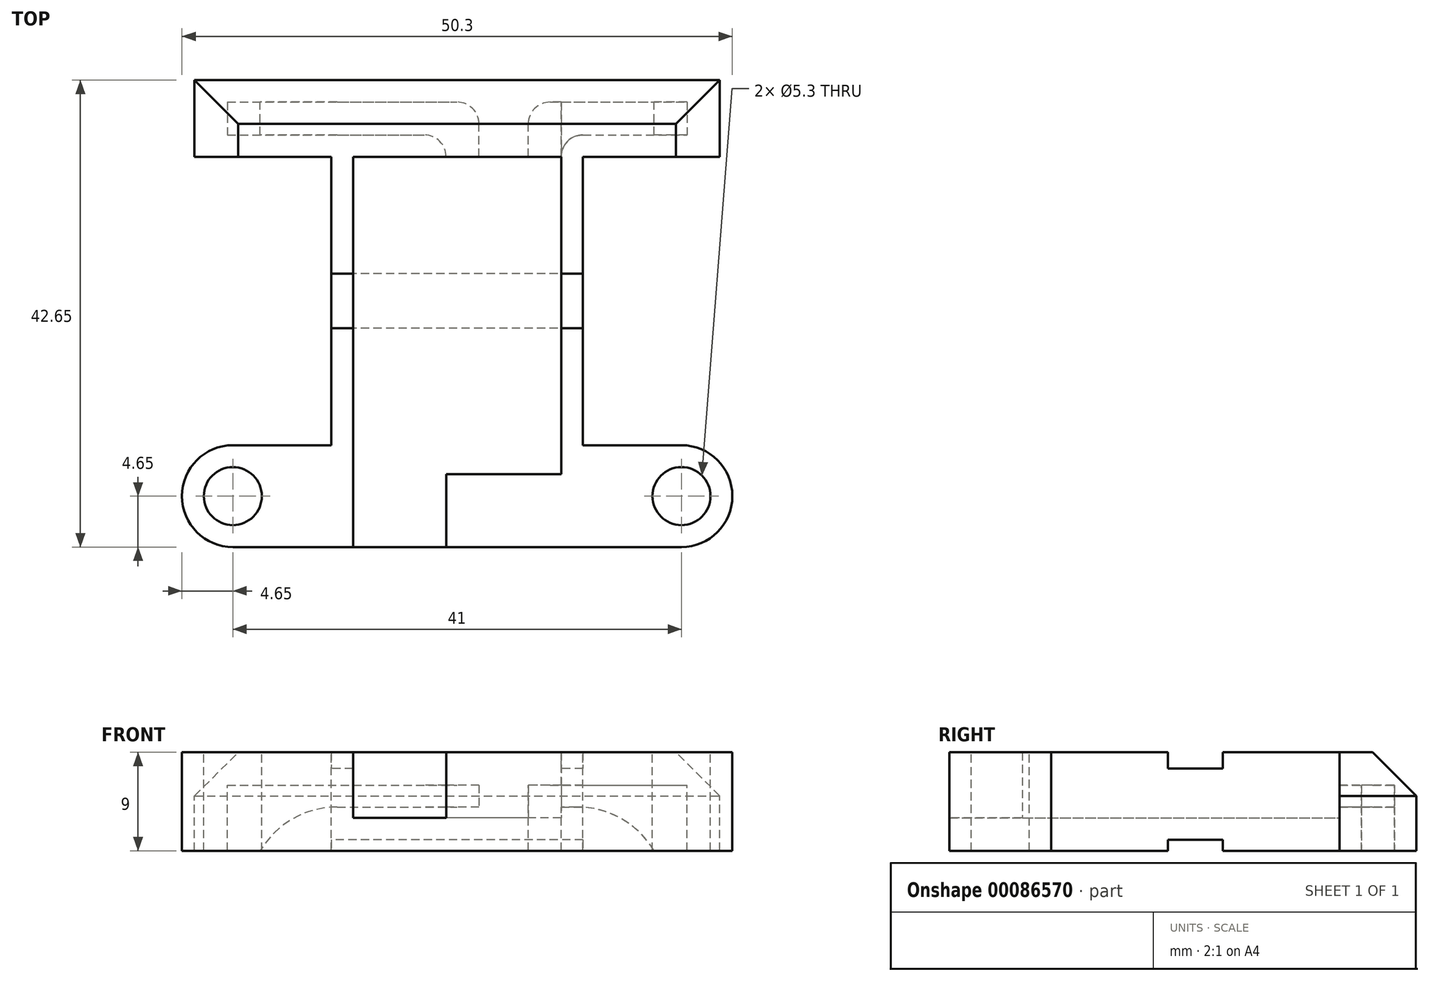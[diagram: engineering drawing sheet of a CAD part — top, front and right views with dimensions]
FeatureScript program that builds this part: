
annotation { "Feature Type Name" : "Feature", "Feature Type Description" : "" }
export const myFeature = defineFeature(function(context is Context, id is Id, definition is map)
    precondition{}
    {
        {
            var Q0;
            Q0=qCreatedBy(makeId("Top.planeOp"),FACE);
            var sketch = newSketch(context, id + "F0", { "sketchPlane" : qUnion([Q0])});
            skLineSegment(sketch, "E0.bottom", {"start": v(9.5, -14.5) * mm, "end": v(-1, -14.5) * mm});
            skLineSegment(sketch, "E0.top", {"start": v(9.5, 14.5) * mm, "end": v(-9.5, 14.5) * mm});
            skLineSegment(sketch, "E0.left", {"start": v(9.5, -14.5) * mm, "end": v(9.5, 14.5) * mm});
            skLineSegment(sketch, "E0.right", {"start": v(-9.5, -21.15) * mm, "end": v(-9.5, 14.5) * mm});
            skPoint(sketch, "E0.middle", {"position": v(0, 0) * mm});
            skLineSegment(sketch, "E1.right", {"start": v(-1, -14.5) * mm, "end": v(-1, -21.15) * mm});
            skLineSegment(sketch, "E2.bottom", {"start": v(-1, 19.5) * mm, "end": v(2, 19.5) * mm});
            skLineSegment(sketch, "E2.top", {"start": v(-1, 14.5) * mm, "end": v(2, 14.5) * mm});
            skLineSegment(sketch, "E2.left", {"start": v(-1, 19.5) * mm, "end": v(-1, 14.5) * mm});
            skLineSegment(sketch, "E2.right", {"start": v(2, 19.5) * mm, "end": v(2, 14.5) * mm});
            skLineSegment(sketch, "E3.bottom", {"start": v(9.5, 14.5) * mm, "end": v(6.5, 14.5) * mm});
            skLineSegment(sketch, "E3.top", {"start": v(9.5, 19.5) * mm, "end": v(6.5, 19.5) * mm});
            skLineSegment(sketch, "E3.left", {"start": v(9.5, 14.5) * mm, "end": v(9.5, 19.5) * mm});
            skLineSegment(sketch, "E3.right", {"start": v(6.5, 14.5) * mm, "end": v(6.5, 19.5) * mm});
            skLineSegment(sketch, "E4.1", {"start": v(20.5, -21.15) * mm, "end": v(-20.5, -21.15) * mm});
            skLineSegment(sketch, "E4.2", {"start": v(11.5, -11.85) * mm, "end": v(11.5, 14.5) * mm});
            skLineSegment(sketch, "E4.4", {"start": v(-11.5, -11.85) * mm, "end": v(-11.5, 14.5) * mm});
            skCircle(sketch, "E5", {"center": v(20.5, -16.5) * mm, "radius": 2.65 * mm});
            skArc(sketch, "E6.0", {"start": v(20.5, -21.15) * mm, "mid": v(25.15, -16.5) * mm, "end": v(20.5, -11.85) * mm});
            skLineSegment(sketch, "E7", {"start": v(11.5, -11.85) * mm, "end": v(20.5, -11.85) * mm});
            skArc(sketch, "E8.MirrorCS", {"start": v(-20.5, -21.15) * mm, "mid": v(-25.15, -16.5) * mm, "end": v(-20.5, -11.85) * mm});
            skCircle(sketch, "E9.MirrorC", {"center": v(-20.5, -16.5) * mm, "radius": 2.65 * mm});
            skLineSegment(sketch, "E10.MirrorCS", {"start": v(-11.5, -11.85) * mm, "end": v(-20.5, -11.85) * mm});
            skLineSegment(sketch, "E11.top", {"start": v(11.5, 14.5) * mm, "end": v(24, 14.5) * mm});
            skLineSegment(sketch, "E11.right", {"start": v(24, 21.5) * mm, "end": v(24, 14.5) * mm});
            skLineSegment(sketch, "E12.MirrorCS", {"start": v(-11.5, 14.5) * mm, "end": v(-24, 14.5) * mm});
            skLineSegment(sketch, "E13.MirrorCS", {"start": v(-24, 21.5) * mm, "end": v(-24, 14.5) * mm});
            skLineSegment(sketch, "E14.MirrorCS", {"start": v(24, 21.5) * mm, "end": v(-24, 21.5) * mm});
            skLineSegment(sketch, "E15.bottom", {"start": v(21, 16.5) * mm, "end": v(18, 16.5) * mm});
            skLineSegment(sketch, "E15.top", {"start": v(21, 19.5) * mm, "end": v(18, 19.5) * mm});
            skLineSegment(sketch, "E15.left", {"start": v(21, 16.5) * mm, "end": v(21, 19.5) * mm});
            skLineSegment(sketch, "E15.right", {"start": v(18, 16.5) * mm, "end": v(18, 19.5) * mm});
            skPoint(sketch, "E15.middle", {"position": v(19.5, 18) * mm});
            skLineSegment(sketch, "E16.MirrorCS", {"start": v(-21, 19.5) * mm, "end": v(-18, 19.5) * mm});
            skLineSegment(sketch, "E17.MirrorCS", {"start": v(-21, 16.5) * mm, "end": v(-21, 19.5) * mm});
            skLineSegment(sketch, "E18.MirrorCS", {"start": v(-21, 16.5) * mm, "end": v(-18, 16.5) * mm});
            skLineSegment(sketch, "E19.MirrorCS", {"start": v(-18, 16.5) * mm, "end": v(-18, 19.5) * mm});
            skPoint(sketch, "E20.MirrorP", {"position": v(-19.5, 18) * mm});
            skPoint(sketch, "E21", {"position": v(24, 18) * mm});
            skSolve(sketch);
        }
        {
            var Q0;
            {var subQ2=sQuery(id+"F0.wireOp",EDGE,"E12.MirrorCS");Q0=makeQuery(id+"F0.imprint","IMPRINT",FACE,{"disambiguationData":[TD([[makeQuery(id+"F0.imprint","IMPRINT",EDGE,{"derivedFrom":subQ2}),-1.0]])]});}
            var Q1;
            Q1=makeQuery(id+"F0.imprint","IMPRINT",FACE,{"disambiguationData":[TD([[makeQuery(id+"F0.imprint","IMPRINT",EDGE,{"derivedFrom":sQuery(id+"F0.wireOp",EDGE,"E0.bottom")}),1.0]])]});
            var Q2;
            Q2=makeQuery(id+"F0.imprint","IMPRINT",FACE,{"disambiguationData":[TD([[makeQuery(id+"F0.imprint","IMPRINT",EDGE,{"derivedFrom":sQuery(id+"F0.wireOp",EDGE,"E0.bottom")}),-1.0]])]});
            var Q3;
            Q3=makeQuery(id+"F0.imprint","IMPRINT",FACE,{"disambiguationData":[TD([[makeQuery(id+"F0.imprint","IMPRINT",EDGE,{"derivedFrom":sQuery(id+"F0.wireOp",EDGE,"E11.bottom")}),-1.0]])]});
            var Q4;
            Q4=makeQuery(id+"F0.imprint","IMPRINT",FACE,{"disambiguationData":[TD([[makeQuery(id+"F0.imprint","IMPRINT",EDGE,{"derivedFrom":sQuery(id+"F0.wireOp",EDGE,"E5")}),-1.0]])]});
            var Q5;
            {var subQ2=sQuery(id+"F0.wireOp",EDGE,"E4.0");Q5=makeQuery(id+"F0.imprint","IMPRINT",FACE,{"disambiguationData":[TD([[makeQuery(id+"F0.imprint","IMPRINT",EDGE,{"derivedFrom":subQ2}),-1.0]])]});}
            var Q6;
            Q6=makeQuery(id+"F0.imprint","IMPRINT",FACE,{"disambiguationData":[TD([[makeQuery(id+"F0.imprint","IMPRINT",EDGE,{"derivedFrom":sQuery(id+"F0.wireOp",EDGE,"E2.bottom")}),-1.0]])]});
            var Q7;
            Q7=makeQuery(id+"F0.imprint","IMPRINT",FACE,{"disambiguationData":[TD([[makeQuery(id+"F0.imprint","IMPRINT",EDGE,{"derivedFrom":sQuery(id+"F0.wireOp",EDGE,"E3.bottom")}),-1.0]])]});
            var Q8;
            {var subQ0=sQuery(id+"F0.wireOp",EDGE,"E8.MirrorCS");Q8=makeQuery(id+"F0.imprint","IMPRINT",FACE,{"disambiguationData":[TD([[makeQuery(id+"F0.imprint","IMPRINT",EDGE,{"derivedFrom":subQ0}),-1.0]])]});}
            extrude(context, id + "F1", {"entities" : qUnion([Q0, Q1, Q2, Q3, Q4, Q5, Q6, Q7, Q8]), "oppositeDirection" : true, "depth" : 3 * mm});
        }
        {
            var Q0;
            Q0=makeQuery(id+"F0.imprint","IMPRINT",FACE,{"disambiguationData":[TD([[makeQuery(id+"F0.imprint","IMPRINT",EDGE,{"derivedFrom":sQuery(id+"F0.wireOp",EDGE,"E0.bottom")}),1.0]])]});
            var Q1;
            {var subQ2=sQuery(id+"F0.wireOp",EDGE,"E12.MirrorCS");Q1=makeQuery(id+"F0.imprint","IMPRINT",FACE,{"disambiguationData":[TD([[makeQuery(id+"F0.imprint","IMPRINT",EDGE,{"derivedFrom":subQ2}),-1.0]])]});}
            var Q2;
            Q2=makeQuery(id+"F0.imprint","IMPRINT",FACE,{"disambiguationData":[TD([[makeQuery(id+"F0.imprint","IMPRINT",EDGE,{"derivedFrom":sQuery(id+"F0.wireOp",EDGE,"E11.bottom")}),-1.0]])]});
            var Q3;
            {var subQ2=sQuery(id+"F0.wireOp",EDGE,"E4.0");Q3=makeQuery(id+"F0.imprint","IMPRINT",FACE,{"disambiguationData":[TD([[makeQuery(id+"F0.imprint","IMPRINT",EDGE,{"derivedFrom":subQ2}),-1.0]])]});}
            var Q4;
            Q4=makeQuery(id+"F0.imprint","IMPRINT",FACE,{"disambiguationData":[TD([[makeQuery(id+"F0.imprint","IMPRINT",EDGE,{"derivedFrom":sQuery(id+"F0.wireOp",EDGE,"E5")}),-1.0]])]});
            var Q5;
            {var subQ0=sQuery(id+"F0.wireOp",EDGE,"E8.MirrorCS");Q5=makeQuery(id+"F0.imprint","IMPRINT",FACE,{"disambiguationData":[TD([[makeQuery(id+"F0.imprint","IMPRINT",EDGE,{"derivedFrom":subQ0}),-1.0]])]});}
            extrude(context, id + "F2", {"entities" : qUnion([Q0, Q1, Q2, Q3, Q4, Q5]), "operationType" : NewBodyOperationType.ADD, "depth" : 6 * mm});
        }
        {
            var Q0;
            Q0=makeQuery(id+"F2.opExtrude","CAP_FACE",FACE,{"disambiguationData":[OSD([sQuery(id+"F0.wireOp",EDGE,"E0.bottom"),sQuery(id+"F0.wireOp",EDGE,"E0.top"),sQuery(id+"F0.wireOp",EDGE,"E0.left"),sQuery(id+"F0.wireOp",EDGE,"E0.right"),sQuery(id+"F0.wireOp",EDGE,"E1.left"),sQuery(id+"F0.wireOp",EDGE,"E1.right"),sQuery(id+"F0.wireOp",EDGE,"E2.bottom"),sQuery(id+"F0.wireOp",EDGE,"E2.left"),sQuery(id+"F0.wireOp",EDGE,"E2.right"),sQuery(id+"F0.wireOp",EDGE,"E3.top"),sQuery(id+"F0.wireOp",EDGE,"E3.left"),sQuery(id+"F0.wireOp",EDGE,"E3.right"),sQuery(id+"F0.wireOp",EDGE,"E4.1"),sQuery(id+"F0.wireOp",EDGE,"E4.2"),sQuery(id+"F0.wireOp",EDGE,"E4.4"),sQuery(id+"F0.wireOp",EDGE,"QdOgvTVK-R7uH-Gxik-RYz1-CrQYq477OOmn"),sQuery(id+"F0.wireOp",EDGE,"E5"),sQuery(id+"F0.wireOp",EDGE,"E6.0"),sQuery(id+"F0.wireOp",EDGE,"E7"),sQuery(id+"F0.wireOp",EDGE,"16d9e2e4-1f67-46e0-b017-a798e0a491060.MirrorCS"),sQuery(id+"F0.wireOp",EDGE,"E8.MirrorCS"),sQuery(id+"F0.wireOp",EDGE,"E9.MirrorC"),sQuery(id+"F0.wireOp",EDGE,"E10.MirrorCS"),sQuery(id+"F0.wireOp",EDGE,"E11.bottom"),sQuery(id+"F0.wireOp",EDGE,"E11.top"),sQuery(id+"F0.wireOp",EDGE,"E11.right"),sQuery(id+"F0.wireOp",EDGE,"mg0W0evk-kMHr-gRv2-KS9r-GgxPjsrzOnwv.bottom"),sQuery(id+"F0.wireOp",EDGE,"mg0W0evk-kMHr-gRv2-KS9r-GgxPjsrzOnwv.top"),sQuery(id+"F0.wireOp",EDGE,"mg0W0evk-kMHr-gRv2-KS9r-GgxPjsrzOnwv.left"),sQuery(id+"F0.wireOp",EDGE,"mg0W0evk-kMHr-gRv2-KS9r-GgxPjsrzOnwv.right"),sQuery(id+"F0.wireOp",EDGE,"E12.MirrorCS"),sQuery(id+"F0.wireOp",EDGE,"E13.MirrorCS"),sQuery(id+"F0.wireOp",EDGE,"E14.MirrorCS"),sQuery(id+"F0.wireOp",EDGE,"11edd65b-5519-47c1-b7c5-a84d8e4c1fdb0.MirrorCS"),sQuery(id+"F0.wireOp",EDGE,"769f5433-8976-4236-af09-d3d3242829100.MirrorCS"),sQuery(id+"F0.wireOp",EDGE,"1cde3c8c-1ea3-4720-a5be-defc2df602b40.MirrorCS"),sQuery(id+"F0.wireOp",EDGE,"8eaebaa9-42e2-4e42-8a77-1a7deb14469b0.MirrorCS")])],"isStart":false});
            cPlane(context, id + "F3", {"entities" : qUnion([Q0]), "cplaneType" : CPlaneType.OFFSET, "offset" : 4 * mm, "oppositeDirection" : true, "width" : 150 * mm, "height" : 150 * mm});
        }
        {
            var Q0;
            Q0=qCreatedBy(id+"F3.planeOp",FACE);
            var sketch = newSketch(context, id + "F4", { "sketchPlane" : qUnion([Q0])});
            skLineSegment(sketch, "E22.bottom", {"start": v(-21, 19.5) * mm, "end": v(2, 19.5) * mm});
            skLineSegment(sketch, "E22.top", {"start": v(-21, 16.5) * mm, "end": v(2, 16.5) * mm});
            skLineSegment(sketch, "E22.left", {"start": v(-21, 19.5) * mm, "end": v(-21, 16.5) * mm});
            skLineSegment(sketch, "E22.right", {"start": v(2, 19.5) * mm, "end": v(2, 16.5) * mm});
            skLineSegment(sketch, "E23.bottom", {"start": v(6.5, 19.5) * mm, "end": v(21, 19.5) * mm});
            skLineSegment(sketch, "E23.top", {"start": v(6.5, 16.5) * mm, "end": v(21, 16.5) * mm});
            skLineSegment(sketch, "E23.left", {"start": v(6.5, 19.5) * mm, "end": v(6.5, 16.5) * mm});
            skLineSegment(sketch, "E23.right", {"start": v(21, 19.5) * mm, "end": v(21, 16.5) * mm});
            skSolve(sketch);
        }
        {
            var Q0;
            Q0=makeQuery(id+"F4.imprint","IMPRINT",FACE,{"disambiguationData":[TD([[makeQuery(id+"F4.imprint","IMPRINT",EDGE,{"derivedFrom":sQuery(id+"F4.wireOp",EDGE,"E22.bottom")}),-1.0]])]});
            var Q1;
            Q1=makeQuery(id+"F4.imprint","IMPRINT",FACE,{"disambiguationData":[TD([[makeQuery(id+"F4.imprint","IMPRINT",EDGE,{"derivedFrom":sQuery(id+"F4.wireOp",EDGE,"E23.bottom")}),-1.0]])]});
            extrude(context, id + "F5", {"entities" : qUnion([Q0, Q1]), "operationType" : NewBodyOperationType.REMOVE, "endBound" : BoundingType.SYMMETRIC, "oppositeDirection" : true, "depth" : 2 * mm});
        }
        {
            var Q0;
            Q0=makeQuery(id+"F2.opExtrude","CAP_FACE",FACE,{"disambiguationData":[OSD([sQuery(id+"F0.wireOp",EDGE,"E0.bottom"),sQuery(id+"F0.wireOp",EDGE,"E0.top"),sQuery(id+"F0.wireOp",EDGE,"E0.left"),sQuery(id+"F0.wireOp",EDGE,"E0.right"),sQuery(id+"F0.wireOp",EDGE,"E1.left"),sQuery(id+"F0.wireOp",EDGE,"E1.right"),sQuery(id+"F0.wireOp",EDGE,"E2.bottom"),sQuery(id+"F0.wireOp",EDGE,"E2.left"),sQuery(id+"F0.wireOp",EDGE,"E2.right"),sQuery(id+"F0.wireOp",EDGE,"E3.top"),sQuery(id+"F0.wireOp",EDGE,"E3.left"),sQuery(id+"F0.wireOp",EDGE,"E3.right"),sQuery(id+"F0.wireOp",EDGE,"E4.1"),sQuery(id+"F0.wireOp",EDGE,"E4.2"),sQuery(id+"F0.wireOp",EDGE,"E4.4"),sQuery(id+"F0.wireOp",EDGE,"QdOgvTVK-R7uH-Gxik-RYz1-CrQYq477OOmn"),sQuery(id+"F0.wireOp",EDGE,"E5"),sQuery(id+"F0.wireOp",EDGE,"E6.0"),sQuery(id+"F0.wireOp",EDGE,"E7"),sQuery(id+"F0.wireOp",EDGE,"16d9e2e4-1f67-46e0-b017-a798e0a491060.MirrorCS"),sQuery(id+"F0.wireOp",EDGE,"E8.MirrorCS"),sQuery(id+"F0.wireOp",EDGE,"E9.MirrorC"),sQuery(id+"F0.wireOp",EDGE,"E10.MirrorCS"),sQuery(id+"F0.wireOp",EDGE,"E11.bottom"),sQuery(id+"F0.wireOp",EDGE,"E11.top"),sQuery(id+"F0.wireOp",EDGE,"E11.right"),sQuery(id+"F0.wireOp",EDGE,"mg0W0evk-kMHr-gRv2-KS9r-GgxPjsrzOnwv.bottom"),sQuery(id+"F0.wireOp",EDGE,"mg0W0evk-kMHr-gRv2-KS9r-GgxPjsrzOnwv.top"),sQuery(id+"F0.wireOp",EDGE,"mg0W0evk-kMHr-gRv2-KS9r-GgxPjsrzOnwv.left"),sQuery(id+"F0.wireOp",EDGE,"mg0W0evk-kMHr-gRv2-KS9r-GgxPjsrzOnwv.right"),sQuery(id+"F0.wireOp",EDGE,"E12.MirrorCS"),sQuery(id+"F0.wireOp",EDGE,"E13.MirrorCS"),sQuery(id+"F0.wireOp",EDGE,"E14.MirrorCS"),sQuery(id+"F0.wireOp",EDGE,"11edd65b-5519-47c1-b7c5-a84d8e4c1fdb0.MirrorCS"),sQuery(id+"F0.wireOp",EDGE,"769f5433-8976-4236-af09-d3d3242829100.MirrorCS"),sQuery(id+"F0.wireOp",EDGE,"1cde3c8c-1ea3-4720-a5be-defc2df602b40.MirrorCS"),sQuery(id+"F0.wireOp",EDGE,"8eaebaa9-42e2-4e42-8a77-1a7deb14469b0.MirrorCS")])],"isStart":false});
            var sketch = newSketch(context, id + "F6", { "sketchPlane" : qUnion([Q0])});
            skLineSegment(sketch, "E24.bottom", {"start": v(18, 19.5) * mm, "end": v(21, 19.5) * mm});
            skLineSegment(sketch, "E24.top", {"start": v(18, 16.5) * mm, "end": v(21, 16.5) * mm});
            skLineSegment(sketch, "E24.left", {"start": v(18, 19.5) * mm, "end": v(18, 16.5) * mm});
            skLineSegment(sketch, "E24.right", {"start": v(21, 19.5) * mm, "end": v(21, 16.5) * mm});
            skLineSegment(sketch, "E25.MirrorCS", {"start": v(-18, 19.5) * mm, "end": v(-18, 16.5) * mm});
            skLineSegment(sketch, "E26.MirrorCS", {"start": v(-18, 19.5) * mm, "end": v(-21, 19.5) * mm});
            skLineSegment(sketch, "E27.MirrorCS", {"start": v(-21, 19.5) * mm, "end": v(-21, 16.5) * mm});
            skLineSegment(sketch, "E28.MirrorCS", {"start": v(-18, 16.5) * mm, "end": v(-21, 16.5) * mm});
            skLineSegment(sketch, "E29.bottom", {"start": v(-1, 19.5) * mm, "end": v(2, 19.5) * mm});
            skLineSegment(sketch, "E29.top", {"start": v(-1, 14.5) * mm, "end": v(2, 14.5) * mm});
            skLineSegment(sketch, "E29.left", {"start": v(-1, 19.5) * mm, "end": v(-1, 14.5) * mm});
            skLineSegment(sketch, "E29.right", {"start": v(2, 19.5) * mm, "end": v(2, 14.5) * mm});
            skLineSegment(sketch, "E30.bottom", {"start": v(6.5, 19.5) * mm, "end": v(9.5, 19.5) * mm});
            skLineSegment(sketch, "E30.top", {"start": v(6.5, 14.5) * mm, "end": v(9.5, 14.5) * mm});
            skLineSegment(sketch, "E30.left", {"start": v(6.5, 19.5) * mm, "end": v(6.5, 14.5) * mm});
            skLineSegment(sketch, "E30.right", {"start": v(9.5, 19.5) * mm, "end": v(9.5, 14.5) * mm});
            skSolve(sketch);
        }
        {
            var Q0;
            Q0=makeQuery(id+"F0.imprint","IMPRINT",FACE,{"disambiguationData":[TD([[makeQuery(id+"F0.imprint","IMPRINT",EDGE,{"derivedFrom":sQuery(id+"F0.wireOp",EDGE,"E2.bottom")}),-1.0]])]});
            var Q1;
            Q1=makeQuery(id+"F0.imprint","IMPRINT",FACE,{"disambiguationData":[TD([[makeQuery(id+"F0.imprint","IMPRINT",EDGE,{"derivedFrom":sQuery(id+"F0.wireOp",EDGE,"E3.bottom")}),-1.0]])]});
            var Q2;
            Q2=makeQuery(id+"F5.boolean.opBoolean","COPY",FACE,{"derivedFrom":makeQuery(id+"F5.opExtrude","CAP_FACE",FACE,{"disambiguationData":[OSD([sQuery(id+"F4.wireOp",EDGE,"E22.bottom"),sQuery(id+"F4.wireOp",EDGE,"E22.top"),sQuery(id+"F4.wireOp",EDGE,"E22.left"),sQuery(id+"F4.wireOp",EDGE,"E22.right")])],"isStart":false})});
            extrude(context, id + "F7", {"entities" : qUnion([Q0, Q1]), "operationType" : NewBodyOperationType.ADD, "endBound" : BoundingType.UP_TO_SURFACE, "endBoundEntityFace" : qUnion([Q2]), "depth" : 25 * mm});
        }
        {
            var Q0;
            Q0=makeQuery(id+"F6.imprint","IMPRINT",FACE,{"disambiguationData":[TD([[makeQuery(id+"F6.imprint","IMPRINT",EDGE,{"derivedFrom":sQuery(id+"F6.wireOp",EDGE,"E24.bottom")}),1.0]])]});
            var Q1;
            Q1=makeQuery(id+"F6.imprint","IMPRINT",FACE,{"disambiguationData":[TD([[makeQuery(id+"F6.imprint","IMPRINT",EDGE,{"derivedFrom":sQuery(id+"F6.wireOp",EDGE,"E25.MirrorCS")}),1.0]])]});
            var Q2;
            Q2=makeQuery(id+"F6.imprint","IMPRINT",FACE,{"disambiguationData":[TD([[makeQuery(id+"F6.imprint","IMPRINT",EDGE,{"derivedFrom":sQuery(id+"F6.wireOp",EDGE,"E29.bottom")}),-1.0]])]});
            var Q3;
            Q3=makeQuery(id+"F6.imprint","IMPRINT",FACE,{"disambiguationData":[TD([[makeQuery(id+"F6.imprint","IMPRINT",EDGE,{"derivedFrom":sQuery(id+"F6.wireOp",EDGE,"E30.bottom")}),1.0]])]});
            var Q4;
            Q4=makeQuery(id+"F5.boolean.opBoolean","COPY",FACE,{"derivedFrom":makeQuery(id+"F5.opExtrude","CAP_FACE",FACE,{"disambiguationData":[OSD([sQuery(id+"F4.wireOp",EDGE,"E22.bottom"),sQuery(id+"F4.wireOp",EDGE,"E22.top"),sQuery(id+"F4.wireOp",EDGE,"E22.left"),sQuery(id+"F4.wireOp",EDGE,"E22.right")])],"isStart":true})});
            extrude(context, id + "F8", {"entities" : qUnion([Q0, Q1, Q2, Q3]), "operationType" : NewBodyOperationType.ADD, "endBound" : BoundingType.UP_TO_SURFACE, "oppositeDirection" : true, "endBoundEntityFace" : qUnion([Q4]), "depth" : 25 * mm});
        }
        {
            var Q0;
            {var subQ0=sQuery(id+"F0.wireOp",EDGE,"E19.MirrorCS");Q0=makeQuery(id+"F5.boolean.opBoolean","INTERSECT",EDGE,{"derivedFrom":[makeQuery(id+"F2.boolean.opBoolean","MERGE",FACE,{"derivedFrom":[makeQuery(id+"F1.opExtrude","SWEPT_FACE",FACE,{"disambiguationData":[OSD([subQ0])]}),makeQuery(id+"F2.opExtrude","SWEPT_FACE",FACE,{"disambiguationData":[OSD([subQ0])]})]}),makeQuery(id+"F5.opExtrude","CAP_FACE",FACE,{"disambiguationData":[OSD([sQuery(id+"F4.wireOp",EDGE,"E22.bottom"),sQuery(id+"F4.wireOp",EDGE,"E22.top"),sQuery(id+"F4.wireOp",EDGE,"E22.left"),sQuery(id+"F4.wireOp",EDGE,"E22.right")])],"isStart":false})]});}
            var Q1;
            Q1=makeQuery(id+"F8.opExtrude","TWEAK_EDGE",EDGE,{"derivedFrom":[makeQuery(id+"F5.boolean.opBoolean","COPY",FACE,{"derivedFrom":makeQuery(id+"F5.opExtrude","CAP_FACE",FACE,{"disambiguationData":[OSD([sQuery(id+"F4.wireOp",EDGE,"E22.bottom"),sQuery(id+"F4.wireOp",EDGE,"E22.top"),sQuery(id+"F4.wireOp",EDGE,"E22.left"),sQuery(id+"F4.wireOp",EDGE,"E22.right")])],"isStart":true})}),makeQuery(id+"F6.imprint","IMPRINT",EDGE,{"derivedFrom":sQuery(id+"F6.wireOp",EDGE,"E27.MirrorCS")})]});
            var Q2;
            {var subQ0=sQuery(id+"F0.wireOp",EDGE,"E15.right");Q2=makeQuery(id+"F5.boolean.opBoolean","INTERSECT",EDGE,{"derivedFrom":[makeQuery(id+"F2.boolean.opBoolean","MERGE",FACE,{"derivedFrom":[makeQuery(id+"F1.opExtrude","SWEPT_FACE",FACE,{"disambiguationData":[OSD([subQ0])]}),makeQuery(id+"F2.opExtrude","SWEPT_FACE",FACE,{"disambiguationData":[OSD([subQ0])]})]}),makeQuery(id+"F5.opExtrude","CAP_FACE",FACE,{"disambiguationData":[OSD([sQuery(id+"F4.wireOp",EDGE,"E23.bottom"),sQuery(id+"F4.wireOp",EDGE,"E23.top"),sQuery(id+"F4.wireOp",EDGE,"E23.left"),sQuery(id+"F4.wireOp",EDGE,"E23.right")])],"isStart":false})]});}
            var Q3;
            Q3=makeQuery(id+"F8.opExtrude","TWEAK_EDGE",EDGE,{"derivedFrom":[makeQuery(id+"F5.boolean.opBoolean","COPY",FACE,{"derivedFrom":makeQuery(id+"F5.opExtrude","CAP_FACE",FACE,{"disambiguationData":[OSD([sQuery(id+"F4.wireOp",EDGE,"E22.bottom"),sQuery(id+"F4.wireOp",EDGE,"E22.top"),sQuery(id+"F4.wireOp",EDGE,"E22.left"),sQuery(id+"F4.wireOp",EDGE,"E22.right")])],"isStart":true})}),makeQuery(id+"F6.imprint","IMPRINT",EDGE,{"derivedFrom":sQuery(id+"F6.wireOp",EDGE,"E24.right")})]});
            fillet(context, id + "F9", {"entities" : qUnion([Q0, Q1, Q2, Q3]), "radius" : 8.2 * mm, "tangentPropagation" : true, "allowEdgeOverflow" : false});
        }
        {
            var Q0;
            Q0=makeQuery(id+"F2.opExtrude","CAP_EDGE",EDGE,{"disambiguationData":[OSD([sQuery(id+"F0.wireOp",EDGE,"E13.MirrorCS")])],"isStart":false});
            var Q1;
            Q1=makeQuery(id+"F2.opExtrude","CAP_EDGE",EDGE,{"disambiguationData":[OSD([sQuery(id+"F0.wireOp",EDGE,"E11.right")])],"isStart":false});
            chamfer(context, id + "F10", {"entities" : qUnion([Q0, Q1]), "width" : 4 * mm, "tangentPropagation" : true});
        }
        {
            var Q0;
            Q0=makeQuery(id+"F5.boolean.opBoolean","INTERSECT",EDGE,{"derivedFrom":[makeQuery(id+"F2.opExtrude","SWEPT_FACE",FACE,{"disambiguationData":[OSD([sQuery(id+"F0.wireOp",EDGE,"E2.left")])]}),makeQuery(id+"F5.opExtrude","SWEPT_FACE",FACE,{"disambiguationData":[OSD([sQuery(id+"F4.wireOp",EDGE,"E22.top")])]})]});
            var Q1;
            Q1=makeQuery(id+"F2.opExtrude","SWEPT_EDGE",EDGE,{"disambiguationData":[OSD([sQuery(id+"F0.wireOp",EDGE,"E2.bottom"),sQuery(id+"F0.wireOp",EDGE,"E2.right")])]});
            var Q2;
            Q2=makeQuery(id+"F2.opExtrude","SWEPT_EDGE",EDGE,{"disambiguationData":[OSD([sQuery(id+"F0.wireOp",EDGE,"E3.top"),sQuery(id+"F0.wireOp",EDGE,"E3.right")])]});
            var Q3;
            Q3=makeQuery(id+"F5.boolean.opBoolean","INTERSECT",EDGE,{"derivedFrom":[makeQuery(id+"F2.opExtrude","SWEPT_FACE",FACE,{"disambiguationData":[OSD([sQuery(id+"F0.wireOp",EDGE,"E0.left"),sQuery(id+"F0.wireOp",EDGE,"E3.left")])]}),makeQuery(id+"F5.opExtrude","SWEPT_FACE",FACE,{"disambiguationData":[OSD([sQuery(id+"F4.wireOp",EDGE,"E23.top")])]})]});
            fillet(context, id + "F11", {"entities" : qUnion([Q0, Q1, Q2, Q3]), "radius" : 2 * mm, "tangentPropagation" : true, "allowEdgeOverflow" : false});
        }
        {
            var Q0;
            {var subQ0=sQuery(id+"F0.wireOp",EDGE,"E4.4");Q0=makeQuery(id+"F2.boolean.opBoolean","MERGE",FACE,{"derivedFrom":[makeQuery(id+"F1.opExtrude","SWEPT_FACE",FACE,{"disambiguationData":[OSD([subQ0])]}),makeQuery(id+"F2.opExtrude","SWEPT_FACE",FACE,{"disambiguationData":[OSD([subQ0])]})]});}
            var sketch = newSketch(context, id + "F12", { "sketchPlane" : qUnion([Q0])});
            skLineSegment(sketch, "E31.bottom", {"start": v(-3.82, -2) * mm, "end": v(1.18, -2) * mm});
            skLineSegment(sketch, "E31.top", {"start": v(-3.82, -3) * mm, "end": v(1.18, -3) * mm});
            skLineSegment(sketch, "E31.left", {"start": v(-3.82, -2) * mm, "end": v(-3.82, -3) * mm});
            skLineSegment(sketch, "E31.right", {"start": v(1.18, -2) * mm, "end": v(1.18, -3) * mm});
            skPoint(sketch, "E32", {"position": v(-1.32, -3) * mm});
            skLineSegment(sketch, "E33.bottom", {"start": v(-3.82, 6) * mm, "end": v(1.17, 6) * mm});
            skLineSegment(sketch, "E33.top", {"start": v(-3.82, 4.5) * mm, "end": v(1.17, 4.5) * mm});
            skLineSegment(sketch, "E33.left", {"start": v(-3.82, 6) * mm, "end": v(-3.82, 4.5) * mm});
            skLineSegment(sketch, "E33.right", {"start": v(1.17, 6) * mm, "end": v(1.17, 4.5) * mm});
            skSolve(sketch);
        }
        {
            var Q0;
            Q0=makeQuery(id+"F12.imprint","IMPRINT",FACE,{"disambiguationData":[TD([[makeQuery(id+"F12.imprint","IMPRINT",EDGE,{"derivedFrom":sQuery(id+"F12.wireOp",EDGE,"E31.bottom")}),-1.0]])]});
            var Q1;
            Q1=makeQuery(id+"F12.imprint","IMPRINT",FACE,{"disambiguationData":[TD([[makeQuery(id+"F12.imprint","IMPRINT",EDGE,{"derivedFrom":sQuery(id+"F12.wireOp",EDGE,"E33.bottom")}),1.0]])]});
            var Q2;
            {var subQ0=sQuery(id+"F0.wireOp",EDGE,"E4.2");Q2=makeQuery(id+"F2.boolean.opBoolean","MERGE",FACE,{"derivedFrom":[makeQuery(id+"F1.opExtrude","SWEPT_FACE",FACE,{"disambiguationData":[OSD([subQ0])]}),makeQuery(id+"F2.opExtrude","SWEPT_FACE",FACE,{"disambiguationData":[OSD([subQ0])]})]});}
            extrude(context, id + "F13", {"entities" : qUnion([Q0, Q1]), "operationType" : NewBodyOperationType.REMOVE, "endBound" : BoundingType.UP_TO_SURFACE, "oppositeDirection" : true, "endBoundEntityFace" : qUnion([Q2]), "depth" : 25 * mm});
        }
        {
            var Q0;
            Q0=makeQuery(id+"F2.opExtrude","CAP_EDGE",EDGE,{"disambiguationData":[OSD([sQuery(id+"F0.wireOp",EDGE,"QdOgvTVK-R7uH-Gxik-RYz1-CrQYq477OOmn"),sQuery(id+"F0.wireOp",EDGE,"E11.bottom"),sQuery(id+"F0.wireOp",EDGE,"E14.MirrorCS")])],"isStart":false});
            chamfer(context, id + "F14", {"entities" : qUnion([Q0]), "width" : 4 * mm, "tangentPropagation" : true});
        }
    });
